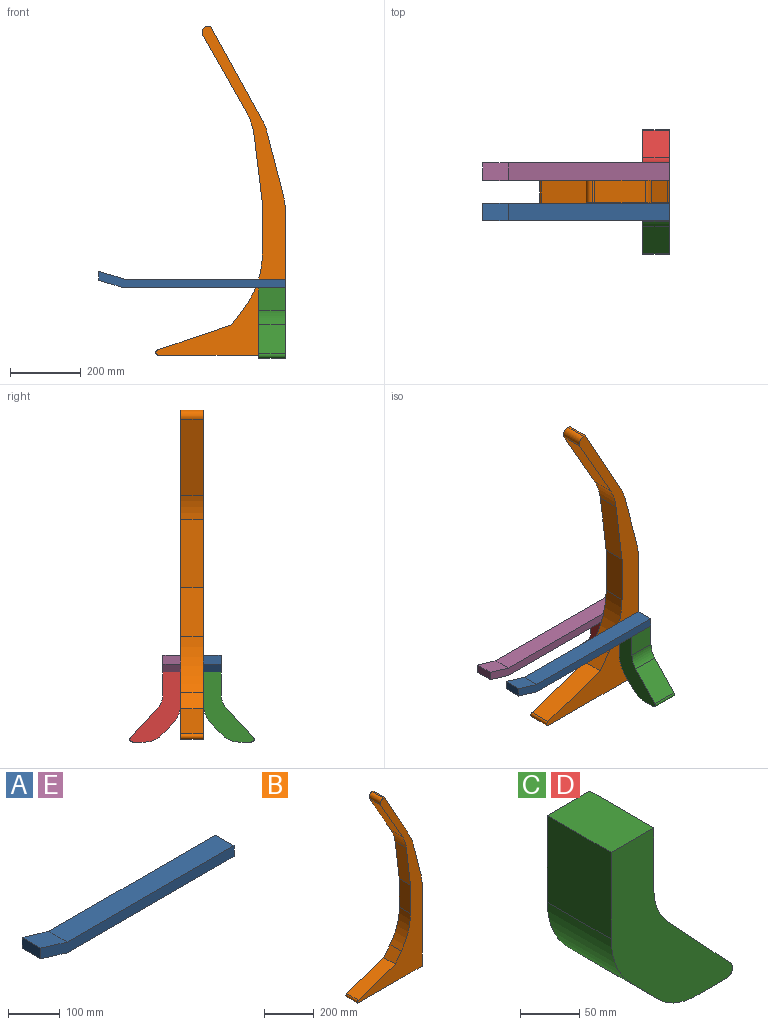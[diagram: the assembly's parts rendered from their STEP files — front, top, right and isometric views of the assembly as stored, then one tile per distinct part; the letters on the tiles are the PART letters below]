
ASSEMBLY  parts=5 mates=4
PART A: 8 faces, bbox 530.2x50.8x47.3 mm
  f0: plane 72.99x50.8mm, normal (0.29,0,0.96), area 3871mm2, adj f1,f5,f6,f7
  f1: plane 50.8x25.4mm, normal (-1,0,0), area 1290.3mm2, adj f0,f2,f6,f7
  f2: plane 72.99x50.8mm, normal (-0.29,0,-0.96), area 3871mm2, adj f1,f3,f6,f7
  f3: plane 457.2x50.8mm, normal (0,0,-1), area 23225.8mm2, adj f2,f4,f6,f7
  f4: plane 50.8x25.4mm, normal (1,0,0), area 1290.3mm2, adj f3,f5,f6,f7
  f5: plane 457.2x50.8mm, normal (0,0,1), area 23225.8mm2, adj f0,f4,f6,f7
  f6: plane 530.19x47.3mm, normal (0,-1,0), area 13466.7mm2, adj f0,f1,f2,f3,f4,f5
  f7: plane 530.19x47.3mm, normal (0,1,0), area 13466.7mm2, adj f0,f1,f2,f3,f4,f5
PART B: 18 faces, bbox 367.5x63.5x933.5 mm
  f0: cylinder r=181.56mm len=63.5mm, axis (0,1,0), area 2904.6mm2, adj f1,f14,f15,f16
  f1: plane 261.26x144.05mm, normal (0.88,0,0.48), area 18944.9mm2, adj f0,f2,f15,f16
  f2: plane 63.5x6.52mm, normal (0,0,1), area 414mm2, adj f1,f15,f16,f17
  f3: plane 216.36x122.99mm, normal (-0.87,0,-0.49), area 15803.6mm2, adj f4,f15,f16,f17
  f4: cylinder r=181.56mm len=67.81mm, axis (0,1,0), area 4564.6mm2, adj f3,f5,f15,f16
  f5: plane 193.51x63.5mm, normal (-0.99,0,-0.12), area 12378.6mm2, adj f4,f6,f15,f16
  f6: plane 139.39x63.5mm, normal (-1,0,0), area 8851.2mm2, adj f5,f7,f15,f16
  f7: cylinder r=263.63mm len=158.2mm, axis (0,1,0), area 10774mm2, adj f6,f8,f15,f16
  f8: plane 63.5x46.04mm, normal (-0.8,0,0.6), area 3654.4mm2, adj f7,f9,f15,f16
  f9: plane 209.73x71.05mm, normal (-0.32,0,0.95), area 14061mm2, adj f8,f10,f15,f16
  f10: cylinder r=7.68mm len=63.5mm, axis (0,1,0), area 1372.1mm2, adj f9,f11,f15,f16
  f11: plane 359.82x63.5mm, normal (0,0,-1), area 22848.4mm2, adj f10,f12,f15,f16
  f12: plane 406.63x63.5mm, normal (1,0,0), area 25820.7mm2, adj f11,f13,f15,f16
  f13: cylinder r=181.56mm len=63.5mm, axis (0,1,0), area 2904.6mm2, adj f12,f14,f15,f16
  f14: plane 177.96x63.5mm, normal (0.97,0,0.25), area 11668.9mm2, adj f0,f13,f15,f16
  f15: plane 933.51x367.49mm, normal (0,-1,0), area 72723.7mm2, adj f0,f1,f2,f3,f4,f5,f6,f7
  f16: plane 933.51x367.49mm, normal (0,1,0), area 72723.7mm2, adj f0,f1,f2,f3,f4,f5,f6,f7
  f17: cylinder r=17.54mm len=63.5mm, axis (0,1,0), area 2325.1mm2, adj f2,f3,f15,f16
PART C: 12 faces, bbox 144.9x76.2x198.6 mm
  f0: plane 76.2x50.8mm, normal (0,0,1), area 3871mm2, adj f1,f9,f10,f11
  f1: plane 89.53x76.2mm, normal (-1,0,0), area 6822.5mm2, adj f0,f2,f10,f11
  f2: cylinder r=81.77mm len=76.2mm, axis (0,1,0), area 4876.8mm2, adj f1,f3,f10,f11
  f3: plane 76.2x32.85mm, normal (-0.71,0,-0.71), area 3530.7mm2, adj f2,f4,f10,f11
  f4: cylinder r=62.92mm len=76.2mm, axis (0,1,0), area 3778.9mm2, adj f3,f5,f10,f11
  f5: plane 76.2x36.41mm, normal (0,0,-1), area 2774.3mm2, adj f4,f6,f10,f11
  f6: cylinder r=7.37mm len=76.2mm, axis (0,1,0), area 1301.4mm2, adj f5,f7,f10,f11
  f7: plane 82.54x76.44mm, normal (0.73,0,0.68), area 8572.3mm2, adj f6,f8,f10,f11
  f8: cylinder r=58.77mm len=76.2mm, axis (0,1,0), area 3345.7mm2, adj f7,f9,f10,f11
  f9: plane 76.2x63.76mm, normal (1,0,0), area 4858.3mm2, adj f0,f8,f10,f11
  f10: plane 198.6x144.86mm, normal (0,-1,0), area 12830.5mm2, adj f0,f1,f2,f3,f4,f5,f6,f7
  f11: plane 198.6x144.86mm, normal (0,1,0), area 12830.5mm2, adj f0,f1,f2,f3,f4,f5,f6,f7
PART D: same geometry as C
PART E: same geometry as A
PLACE A t=(-262.38,-493.76,-4.95)mm
PLACE B t=(60.59,-430.26,199.79)mm
PLACE C rot(axis=(0,0,-1),90deg) t=(213.15,-588.12,-121.15)mm
PLACE D rot(axis=(0,0,1),90deg) t=(136.95,-335.9,-121.15)mm
PLACE E t=(-262.38,-379.46,-4.95)mm
MATE fastened A.f3 <-> C.f0  axis (0,0,-1) through (213.15,-493.76,-34.36)mm
MATE fastened E.f3 <-> D.f0  axis (0,0,-1) through (213.15,-430.26,-34.36)mm
MATE fastened B.f15 <-> A.f7  axis (0,-1,0) through (213.15,-493.76,-21.66)mm
MATE fastened E.f6 <-> B.f16  axis (0,-1,0) through (213.15,-430.26,-21.66)mm
